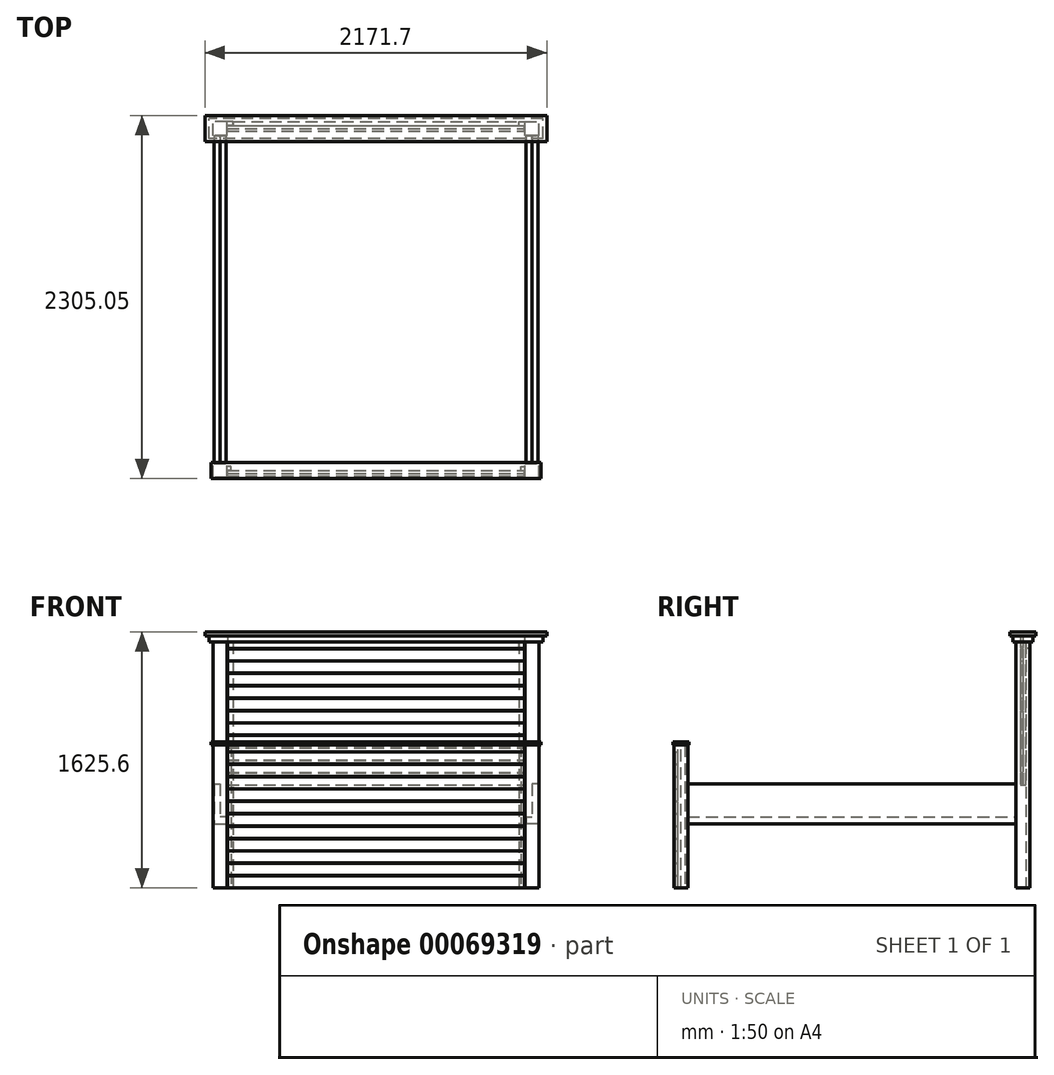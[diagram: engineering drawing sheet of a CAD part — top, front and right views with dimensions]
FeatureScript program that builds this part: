
annotation { "Feature Type Name" : "Feature", "Feature Type Description" : "" }
export const myFeature = defineFeature(function(context is Context, id is Id, definition is map)
    precondition{}
    {
        {
            var Q0;
            Q0=qCreatedBy(makeId("Top.planeOp"),FACE);
            var sketch = newSketch(context, id + "F0", { "sketchPlane" : qUnion([Q0])});
            skLineSegment(sketch, "E0.rect.bottom", {"start": v(44.45, -44.45) * mm, "end": v(-44.45, -44.45) * mm});
            skLineSegment(sketch, "E0.rect.top", {"start": v(44.45, 44.45) * mm, "end": v(-44.45, 44.45) * mm});
            skLineSegment(sketch, "E0.rect.left", {"start": v(44.45, -44.45) * mm, "end": v(44.45, 44.45) * mm});
            skLineSegment(sketch, "E0.rect.right", {"start": v(-44.45, -44.45) * mm, "end": v(-44.45, 44.45) * mm});
            skPoint(sketch, "E0.rect.middle", {"position": v(0, 0) * mm});
            skSolve(sketch);
        }
        {
            var Q0;
            Q0 = qSketchRegion(id + "F0", true);
            extrude(context, id + "F1", {"entities" : qUnion([Q0]), "depth" : 906.78 * mm});
        }
        {
            var Q0;
            Q0=makeQuery(id+"F1.opExtrude","SWEPT_FACE",FACE,{"disambiguationData":[OSD([sQuery(id+"F0.wireOp",EDGE,"E0.rect.left")])]});
            var sketch = newSketch(context, id + "F2", { "sketchPlane" : qUnion([Q0])});
            skLineSegment(sketch, "E1.bottom", {"start": v(0, 906.78) * mm, "end": v(25.4, 906.78) * mm});
            skLineSegment(sketch, "E1.top", {"start": v(0, 0) * mm, "end": v(25.4, 0) * mm});
            skLineSegment(sketch, "E1.left", {"start": v(0, 906.78) * mm, "end": v(0, 0) * mm});
            skLineSegment(sketch, "E1.right", {"start": v(25.4, 906.78) * mm, "end": v(25.4, 0) * mm});
            skSolve(sketch);
        }
        {
            var Q0;
            Q0 = qSketchRegion(id + "F2", true);
            extrude(context, id + "F3", {"entities" : qUnion([Q0]), "depth" : 25.4 * mm});
        }
        {
            var Q0;
            Q0=qCreatedBy(makeId("Right.planeOp"),FACE);
            cPlane(context, id + "F4", {"entities" : qUnion([Q0]), "cplaneType" : CPlaneType.OFFSET, "offset" : 990.6 * mm, "width" : 152.4 * mm, "height" : 152.4 * mm});
        }
        {
            var Q0;
            Q0=makeQuery(id+"F1.opExtrude","SWEPT_BODY",BODY,{"disambiguationData":[OSD([sQuery(id+"F0.wireOp",EDGE,"E0.rect.bottom"),sQuery(id+"F0.wireOp",EDGE,"E0.rect.top"),sQuery(id+"F0.wireOp",EDGE,"E0.rect.left"),sQuery(id+"F0.wireOp",EDGE,"E0.rect.right")])]});
            var Q1;
            Q1=makeQuery(id+"F3.opExtrude","SWEPT_BODY",BODY,{"disambiguationData":[OSD([sQuery(id+"F2.wireOp",EDGE,"E1.bottom"),sQuery(id+"F2.wireOp",EDGE,"E1.top"),sQuery(id+"F2.wireOp",EDGE,"E1.left"),sQuery(id+"F2.wireOp",EDGE,"E1.right")])]});
            var Q2;
            Q2=qCreatedBy(id+"F4.planeOp",FACE);
            mirror(context, id + "F5", {"entities" : qUnion([Q0, Q1]), "mirrorPlane" : qUnion([Q2])});
        }
        {
            var Q0;
            Q0=makeQuery(id+"F1.opExtrude","CAP_FACE",FACE,{"disambiguationData":[OSD([sQuery(id+"F0.wireOp",EDGE,"E0.rect.bottom"),sQuery(id+"F0.wireOp",EDGE,"E0.rect.top"),sQuery(id+"F0.wireOp",EDGE,"E0.rect.left"),sQuery(id+"F0.wireOp",EDGE,"E0.rect.right")])],"isStart":false});
            var sketch = newSketch(context, id + "F6", { "sketchPlane" : qUnion([Q0])});
            skLineSegment(sketch, "E2", {"start": v(0, 0) * mm, "end": v(1981.2, 0) * mm, "construction": true});
            skPoint(sketch, "E2.endSnap0", {"position": v(44.45, 0) * mm});
            skLineSegment(sketch, "E3", {"start": v(1936.75, 44.45) * mm, "end": v(2025.65, -44.45) * mm, "construction": true});
            skLineSegment(sketch, "E4.rect.bottom", {"start": v(-57.15, -50.8) * mm, "end": v(2038.35, -50.8) * mm});
            skLineSegment(sketch, "E4.rect.top", {"start": v(-57.15, 50.8) * mm, "end": v(2038.35, 50.8) * mm});
            skLineSegment(sketch, "E4.rect.left", {"start": v(-57.15, -50.8) * mm, "end": v(-57.15, 50.8) * mm});
            skLineSegment(sketch, "E4.rect.right", {"start": v(2038.35, -50.8) * mm, "end": v(2038.35, 50.8) * mm});
            skPoint(sketch, "E4.rect.middle", {"position": v(990.6, 0) * mm});
            skSolve(sketch);
        }
        {
            var Q0;
            Q0 = qSketchRegion(id + "F6", true);
            extrude(context, id + "F7", {"entities" : qUnion([Q0]), "depth" : 19.05 * mm});
        }
        {
            var Q0;
            Q0=makeQuery(id+"F3.opExtrude","SWEPT_FACE",FACE,{"disambiguationData":[OSD([sQuery(id+"F2.wireOp",EDGE,"E1.left")])]});
            var sketch = newSketch(context, id + "F8", { "sketchPlane" : qUnion([Q0])});
            skLineSegment(sketch, "E5", {"start": v(44.45, 906.78) * mm, "end": v(1936.75, 0) * mm, "construction": true});
            skLineSegment(sketch, "E6.rect.bottom", {"start": v(46.99, 0) * mm, "end": v(1934.2, 0) * mm});
            skLineSegment(sketch, "E6.rect.top", {"start": v(46.99, 906.78) * mm, "end": v(1934.21, 906.78) * mm});
            skLineSegment(sketch, "E6.rect.left", {"start": v(47, 0) * mm, "end": v(47, 906.78) * mm});
            skLineSegment(sketch, "E6.rect.right", {"start": v(1934.2, 0) * mm, "end": v(1934.2, 906.78) * mm});
            skPoint(sketch, "E6.rect.middle", {"position": v(990.6, 453.4) * mm});
            skSolve(sketch);
        }
        {
            var Q0;
            Q0 = qSketchRegion(id + "F8", true);
            extrude(context, id + "F9", {"entities" : qUnion([Q0]), "depth" : 19.05 * mm});
        }
        {
            var Q0;
            Q0=makeQuery(id+"F9.opExtrude","CAP_FACE",FACE,{"disambiguationData":[OSD([sQuery(id+"F8.wireOp",EDGE,"E6.rect.bottom"),sQuery(id+"F8.wireOp",EDGE,"E6.rect.top"),sQuery(id+"F8.wireOp",EDGE,"E6.rect.left"),sQuery(id+"F8.wireOp",EDGE,"E6.rect.right")])],"isStart":false});
            var sketch = newSketch(context, id + "F10", { "sketchPlane" : qUnion([Q0])});
            skLineSegment(sketch, "E7.bottom", {"start": v(46.99, 76.2) * mm, "end": v(1934.2, 76.2) * mm});
            skLineSegment(sketch, "E7.top", {"start": v(46.99, 0) * mm, "end": v(1934.2, 0) * mm});
            skLineSegment(sketch, "E7.left", {"start": v(47, 76.2) * mm, "end": v(47, 0) * mm});
            skLineSegment(sketch, "E7.right", {"start": v(1934.2, 76.2) * mm, "end": v(1934.2, 0) * mm});
            skLineSegment(sketch, "E8.0.1.0", {"start": v(47, 154.94) * mm, "end": v(47, 78.74) * mm});
            skLineSegment(sketch, "E8.0.1.1", {"start": v(46.99, 154.94) * mm, "end": v(1934.2, 154.94) * mm});
            skLineSegment(sketch, "E8.0.1.2", {"start": v(46.99, 78.74) * mm, "end": v(1934.2, 78.74) * mm});
            skLineSegment(sketch, "E8.0.1.3", {"start": v(1934.2, 154.94) * mm, "end": v(1934.2, 78.74) * mm});
            skLineSegment(sketch, "E8.0.2.0", {"start": v(47, 233.68) * mm, "end": v(47, 157.48) * mm});
            skLineSegment(sketch, "E8.0.2.1", {"start": v(46.99, 233.68) * mm, "end": v(1934.2, 233.68) * mm});
            skLineSegment(sketch, "E8.0.2.2", {"start": v(46.99, 157.48) * mm, "end": v(1934.2, 157.48) * mm});
            skLineSegment(sketch, "E8.0.2.3", {"start": v(1934.2, 233.68) * mm, "end": v(1934.2, 157.48) * mm});
            skLineSegment(sketch, "E8.0.3.0", {"start": v(47, 312.42) * mm, "end": v(47, 236.22) * mm});
            skLineSegment(sketch, "E8.0.3.1", {"start": v(46.99, 312.42) * mm, "end": v(1934.2, 312.42) * mm});
            skLineSegment(sketch, "E8.0.3.2", {"start": v(46.99, 236.22) * mm, "end": v(1934.2, 236.22) * mm});
            skLineSegment(sketch, "E8.0.3.3", {"start": v(1934.2, 312.42) * mm, "end": v(1934.2, 236.22) * mm});
            skLineSegment(sketch, "E8.0.4.0", {"start": v(47, 391.16) * mm, "end": v(47, 314.96) * mm});
            skLineSegment(sketch, "E8.0.4.1", {"start": v(46.99, 391.16) * mm, "end": v(1934.2, 391.16) * mm});
            skLineSegment(sketch, "E8.0.4.2", {"start": v(46.99, 314.96) * mm, "end": v(1934.2, 314.96) * mm});
            skLineSegment(sketch, "E8.0.4.3", {"start": v(1934.2, 391.16) * mm, "end": v(1934.2, 314.96) * mm});
            skLineSegment(sketch, "E8.0.5.0", {"start": v(47, 469.9) * mm, "end": v(47, 393.7) * mm});
            skLineSegment(sketch, "E8.0.5.1", {"start": v(46.99, 469.9) * mm, "end": v(1934.2, 469.9) * mm});
            skLineSegment(sketch, "E8.0.5.2", {"start": v(46.99, 393.7) * mm, "end": v(1934.2, 393.7) * mm});
            skLineSegment(sketch, "E8.0.5.3", {"start": v(1934.2, 469.9) * mm, "end": v(1934.2, 393.7) * mm});
            skLineSegment(sketch, "E8.direction1", {"start": v(47, 0) * mm, "end": v(72.4, 0) * mm, "construction": true});
            skLineSegment(sketch, "E8.direction2", {"start": v(47, 0) * mm, "end": v(47, 78.74) * mm, "construction": true});
            skLineSegment(sketch, "E9.0.0.6", {"start": v(47, 548.64) * mm, "end": v(47, 472.44) * mm});
            skLineSegment(sketch, "E9.3.0.6", {"start": v(46.99, 548.64) * mm, "end": v(1934.2, 548.64) * mm});
            skLineSegment(sketch, "E9.6.0.6", {"start": v(46.99, 472.44) * mm, "end": v(1934.2, 472.44) * mm});
            skLineSegment(sketch, "E9.9.0.6", {"start": v(1934.2, 548.64) * mm, "end": v(1934.2, 472.44) * mm});
            skLineSegment(sketch, "E10.0.0.7", {"start": v(47, 627.38) * mm, "end": v(47, 551.18) * mm});
            skLineSegment(sketch, "E10.3.0.7", {"start": v(46.99, 627.38) * mm, "end": v(1934.2, 627.38) * mm});
            skLineSegment(sketch, "E10.6.0.7", {"start": v(46.99, 551.18) * mm, "end": v(1934.2, 551.18) * mm});
            skLineSegment(sketch, "E10.9.0.7", {"start": v(1934.2, 627.38) * mm, "end": v(1934.2, 551.18) * mm});
            skLineSegment(sketch, "E10.0.0.8", {"start": v(47, 706.12) * mm, "end": v(47, 629.92) * mm});
            skLineSegment(sketch, "E10.3.0.8", {"start": v(46.99, 706.12) * mm, "end": v(1934.2, 706.12) * mm});
            skLineSegment(sketch, "E10.6.0.8", {"start": v(46.99, 629.92) * mm, "end": v(1934.2, 629.92) * mm});
            skLineSegment(sketch, "E10.9.0.8", {"start": v(1934.2, 706.12) * mm, "end": v(1934.2, 629.92) * mm});
            skLineSegment(sketch, "E10.0.0.9", {"start": v(47, 784.86) * mm, "end": v(47, 708.66) * mm});
            skLineSegment(sketch, "E10.3.0.9", {"start": v(46.99, 784.86) * mm, "end": v(1934.2, 784.86) * mm});
            skLineSegment(sketch, "E10.6.0.9", {"start": v(46.99, 708.66) * mm, "end": v(1934.2, 708.66) * mm});
            skLineSegment(sketch, "E10.9.0.9", {"start": v(1934.2, 784.86) * mm, "end": v(1934.2, 708.66) * mm});
            skLineSegment(sketch, "E11.0.0.10", {"start": v(47, 863.6) * mm, "end": v(47, 787.4) * mm});
            skLineSegment(sketch, "E11.3.0.10", {"start": v(46.99, 863.6) * mm, "end": v(1934.2, 863.6) * mm});
            skLineSegment(sketch, "E11.6.0.10", {"start": v(46.99, 787.4) * mm, "end": v(1934.2, 787.4) * mm});
            skLineSegment(sketch, "E11.9.0.10", {"start": v(1934.2, 863.6) * mm, "end": v(1934.2, 787.4) * mm});
            skSolve(sketch);
        }
        {
            var Q0;
            Q0 = qSketchRegion(id + "F10", true);
            extrude(context, id + "F11", {"entities" : qUnion([Q0]), "depth" : 15.88 * mm});
        }
        {
            var Q0;
            Q0=makeQuery(id+"F1.opExtrude","SWEPT_FACE",FACE,{"disambiguationData":[OSD([sQuery(id+"F0.wireOp",EDGE,"E0.rect.top")])]});
            var sketch = newSketch(context, id + "F12", { "sketchPlane" : qUnion([Q0])});
            skLineSegment(sketch, "E12.bottom", {"start": v(38.1, 660.4) * mm, "end": v(0, 660.4) * mm});
            skLineSegment(sketch, "E12.top", {"start": v(38.1, 406.4) * mm, "end": v(0, 406.4) * mm});
            skLineSegment(sketch, "E12.left", {"start": v(38.1, 660.4) * mm, "end": v(38.1, 406.4) * mm});
            skLineSegment(sketch, "E12.right", {"start": v(0, 660.4) * mm, "end": v(0, 406.4) * mm});
            skSolve(sketch);
        }
        {
            var Q0;
            Q0 = qSketchRegion(id + "F12", true);
            extrude(context, id + "F13", {"entities" : qUnion([Q0]), "depth" : 2082.8 * mm});
        }
        {
            var Q0;
            Q0=makeQuery(id+"F13.opExtrude","SWEPT_FACE",FACE,{"disambiguationData":[OSD([sQuery(id+"F12.wireOp",EDGE,"E12.right")])]});
            var sketch = newSketch(context, id + "F14", { "sketchPlane" : qUnion([Q0])});
            skLineSegment(sketch, "E13.bottom", {"start": v(44.45, 450.85) * mm, "end": v(2127.25, 450.85) * mm});
            skLineSegment(sketch, "E13.top", {"start": v(44.45, 406.4) * mm, "end": v(2127.25, 406.4) * mm});
            skLineSegment(sketch, "E13.left", {"start": v(44.45, 450.85) * mm, "end": v(44.45, 406.4) * mm});
            skLineSegment(sketch, "E13.right", {"start": v(2127.25, 450.85) * mm, "end": v(2127.25, 406.4) * mm});
            skSolve(sketch);
        }
        {
            var Q0;
            Q0 = qSketchRegion(id + "F14", true);
            extrude(context, id + "F15", {"entities" : qUnion([Q0]), "depth" : 38.1 * mm});
        }
        {
            var Q0;
            Q0=makeQuery(id+"F13.opExtrude","SWEPT_BODY",BODY,{"disambiguationData":[OSD([sQuery(id+"F12.wireOp",EDGE,"E12.bottom"),sQuery(id+"F12.wireOp",EDGE,"E12.top"),sQuery(id+"F12.wireOp",EDGE,"E12.left"),sQuery(id+"F12.wireOp",EDGE,"E12.right")])]});
            var Q1;
            Q1=makeQuery(id+"F15.opExtrude","SWEPT_BODY",BODY,{"disambiguationData":[OSD([sQuery(id+"F14.wireOp",EDGE,"E13.bottom"),sQuery(id+"F14.wireOp",EDGE,"E13.top"),sQuery(id+"F14.wireOp",EDGE,"E13.left"),sQuery(id+"F14.wireOp",EDGE,"E13.right")])]});
            var Q2;
            Q2=qCreatedBy(id+"F4.planeOp",FACE);
            mirror(context, id + "F16", {"operationType" : NewBodyOperationType.ADD, "entities" : qUnion([Q0, Q1]), "mirrorPlane" : qUnion([Q2])});
        }
        {
            var Q0;
            Q0=qCreatedBy(makeId("Top.planeOp"),FACE);
            var sketch = newSketch(context, id + "F17", { "sketchPlane" : qUnion([Q0])});
            skLineSegment(sketch, "E14.rect.bottom", {"start": v(44.45, 2127.25) * mm, "end": v(-44.45, 2127.25) * mm});
            skLineSegment(sketch, "E14.rect.top", {"start": v(44.45, 2216.15) * mm, "end": v(-44.45, 2216.15) * mm});
            skLineSegment(sketch, "E14.rect.left", {"start": v(44.45, 2127.25) * mm, "end": v(44.45, 2216.15) * mm});
            skLineSegment(sketch, "E14.rect.right", {"start": v(-44.45, 2127.25) * mm, "end": v(-44.45, 2216.15) * mm});
            skPoint(sketch, "E14.rect.middle", {"position": v(0, 2171.7) * mm});
            skLineSegment(sketch, "E15.rect.bottom", {"start": v(1936.75, 2127.25) * mm, "end": v(2025.65, 2127.25) * mm});
            skLineSegment(sketch, "E15.rect.top", {"start": v(1936.75, 2216.15) * mm, "end": v(2025.65, 2216.15) * mm});
            skLineSegment(sketch, "E15.rect.left", {"start": v(1936.75, 2127.25) * mm, "end": v(1936.75, 2216.15) * mm});
            skLineSegment(sketch, "E15.rect.right", {"start": v(2025.65, 2127.25) * mm, "end": v(2025.65, 2216.15) * mm});
            skPoint(sketch, "E15.rect.middle", {"position": v(1981.2, 2171.7) * mm});
            skSolve(sketch);
        }
        {
            var Q0;
            Q0 = qSketchRegion(id + "F17", true);
            extrude(context, id + "F18", {"entities" : qUnion([Q0]), "depth" : 1562.1 * mm});
        }
        {
            var Q0;
            Q0=makeQuery(id+"F18.opExtrude","SWEPT_FACE",FACE,{"disambiguationData":[OSD([sQuery(id+"F17.wireOp",EDGE,"E14.rect.left")])]});
            var sketch = newSketch(context, id + "F19", { "sketchPlane" : qUnion([Q0])});
            skLineSegment(sketch, "E16.bottom", {"start": v(2216.15, 1562.1) * mm, "end": v(2190.75, 1562.1) * mm});
            skLineSegment(sketch, "E16.top", {"start": v(2216.15, 0) * mm, "end": v(2171.7, 0) * mm});
            skLineSegment(sketch, "E16.left", {"start": v(2216.15, 1562.1) * mm, "end": v(2216.15, 0) * mm});
            skLineSegment(sketch, "E16.right", {"start": v(2190.75, 1562.1) * mm, "end": v(2190.75, 0) * mm});
            skSolve(sketch);
        }
        {
            var Q0;
            Q0 = qSketchRegion(id + "F19", true);
            extrude(context, id + "F20", {"entities" : qUnion([Q0]), "depth" : 38.1 * mm});
        }
        {
            var Q0;
            Q0=makeQuery(id+"F20.opExtrude","SWEPT_BODY",BODY,{"disambiguationData":[OSD([sQuery(id+"F19.wireOp",EDGE,"E16.bottom"),sQuery(id+"F19.wireOp",EDGE,"E16.top"),sQuery(id+"F19.wireOp",EDGE,"E16.left"),sQuery(id+"F19.wireOp",EDGE,"E16.right")])]});
            var Q1;
            Q1=qCreatedBy(id+"F4.planeOp",FACE);
            mirror(context, id + "F21", {"entities" : qUnion([Q0]), "mirrorPlane" : qUnion([Q1])});
        }
        {
            var Q0;
            Q0=makeQuery(id+"F18.opExtrude","CAP_FACE",FACE,{"disambiguationData":[OSD([sQuery(id+"F17.wireOp",EDGE,"E14.rect.bottom"),sQuery(id+"F17.wireOp",EDGE,"E14.rect.top"),sQuery(id+"F17.wireOp",EDGE,"E14.rect.left"),sQuery(id+"F17.wireOp",EDGE,"E14.rect.right")])],"isStart":false});
            var sketch = newSketch(context, id + "F22", { "sketchPlane" : qUnion([Q0])});
            skLineSegment(sketch, "E17", {"start": v(44.45, 2171.7) * mm, "end": v(1936.75, 2171.7) * mm, "construction": true});
            skPoint(sketch, "E17.endSnap0", {"position": v(44.45, 2171.7) * mm});
            skLineSegment(sketch, "E18.rect.bottom", {"start": v(2051.05, 2108.2) * mm, "end": v(-69.85, 2108.2) * mm});
            skLineSegment(sketch, "E18.rect.top", {"start": v(2051.05, 2235.2) * mm, "end": v(-69.85, 2235.2) * mm});
            skLineSegment(sketch, "E18.rect.left", {"start": v(2051.05, 2108.2) * mm, "end": v(2051.05, 2235.2) * mm});
            skLineSegment(sketch, "E18.rect.right", {"start": v(-69.85, 2108.2) * mm, "end": v(-69.85, 2235.2) * mm});
            skPoint(sketch, "E18.rect.middle", {"position": v(990.6, 2171.7) * mm});
            skSolve(sketch);
        }
        {
            var Q0;
            Q0 = qSketchRegion(id + "F22", true);
            extrude(context, id + "F23", {"entities" : qUnion([Q0]), "depth" : 38.1 * mm});
        }
        {
            var Q0;
            Q0=makeQuery(id+"F23.opExtrude","CAP_FACE",FACE,{"disambiguationData":[OSD([sQuery(id+"F22.wireOp",EDGE,"E18.rect.bottom"),sQuery(id+"F22.wireOp",EDGE,"E18.rect.top"),sQuery(id+"F22.wireOp",EDGE,"E18.rect.left"),sQuery(id+"F22.wireOp",EDGE,"E18.rect.right")])],"isStart":true});
            var sketch = newSketch(context, id + "F24", { "sketchPlane" : qUnion([Q0])});
            skLineSegment(sketch, "E19.bottom", {"start": v(85.1, -2190.75) * mm, "end": v(1898.65, -2190.75) * mm});
            skLineSegment(sketch, "E19.top", {"start": v(85.1, -2216.15) * mm, "end": v(1898.65, -2216.15) * mm});
            skLineSegment(sketch, "E19.left", {"start": v(85.1, -2190.75) * mm, "end": v(85.1, -2216.15) * mm});
            skLineSegment(sketch, "E19.right", {"start": v(1898.65, -2190.75) * mm, "end": v(1898.65, -2216.15) * mm});
            skSolve(sketch);
        }
        {
            var Q0;
            Q0 = qSketchRegion(id + "F24", true);
            extrude(context, id + "F25", {"entities" : qUnion([Q0]), "depth" : 38.1 * mm});
        }
        {
            var Q0;
            Q0=makeQuery(id+"F20.opExtrude","SWEPT_FACE",FACE,{"disambiguationData":[OSD([sQuery(id+"F19.wireOp",EDGE,"E16.right")])]});
            var sketch = newSketch(context, id + "F26", { "sketchPlane" : qUnion([Q0])});
            skLineSegment(sketch, "E20", {"start": v(44.45, 1562.1) * mm, "end": v(1936.75, 654.05) * mm, "construction": true});
            skLineSegment(sketch, "E21.rect.bottom", {"start": v(46.04, 655.64) * mm, "end": v(1935.16, 655.64) * mm});
            skLineSegment(sketch, "E21.rect.top", {"start": v(46.04, 1560.51) * mm, "end": v(1935.16, 1560.51) * mm});
            skLineSegment(sketch, "E21.rect.left", {"start": v(46.04, 655.64) * mm, "end": v(46.04, 1560.51) * mm});
            skLineSegment(sketch, "E21.rect.right", {"start": v(1935.16, 655.64) * mm, "end": v(1935.16, 1560.51) * mm});
            skPoint(sketch, "E21.rect.middle", {"position": v(990.6, 1108.07) * mm});
            skSolve(sketch);
        }
        {
            var Q0;
            Q0 = qSketchRegion(id + "F26", true);
            extrude(context, id + "F27", {"entities" : qUnion([Q0]), "depth" : 19.05 * mm});
        }
        {
            var Q0;
            Q0=makeQuery(id+"F27.opExtrude","CAP_FACE",FACE,{"disambiguationData":[OSD([sQuery(id+"F26.wireOp",EDGE,"E21.rect.bottom"),sQuery(id+"F26.wireOp",EDGE,"E21.rect.top"),sQuery(id+"F26.wireOp",EDGE,"E21.rect.left"),sQuery(id+"F26.wireOp",EDGE,"E21.rect.right")])],"isStart":false});
            var sketch = newSketch(context, id + "F28", { "sketchPlane" : qUnion([Q0])});
            skLineSegment(sketch, "E22.bottom", {"start": v(47, 731.84) * mm, "end": v(1934.21, 731.84) * mm});
            skLineSegment(sketch, "E22.top", {"start": v(46.99, 655.64) * mm, "end": v(1934.21, 655.64) * mm});
            skLineSegment(sketch, "E22.left", {"start": v(46.99, 731.84) * mm, "end": v(46.99, 655.64) * mm});
            skLineSegment(sketch, "E22.right", {"start": v(1934.21, 731.84) * mm, "end": v(1934.21, 655.64) * mm});
            skLineSegment(sketch, "E23.0.1.0", {"start": v(46.99, 810.58) * mm, "end": v(1934.21, 810.58) * mm});
            skLineSegment(sketch, "E23.0.1.1", {"start": v(1934.21, 810.58) * mm, "end": v(1934.21, 734.38) * mm});
            skLineSegment(sketch, "E23.0.1.2", {"start": v(47, 734.38) * mm, "end": v(1934.21, 734.38) * mm});
            skLineSegment(sketch, "E23.0.1.3", {"start": v(46.99, 810.58) * mm, "end": v(46.99, 734.38) * mm});
            skLineSegment(sketch, "E23.0.2.0", {"start": v(46.99, 889.32) * mm, "end": v(1934.21, 889.32) * mm});
            skLineSegment(sketch, "E23.0.2.1", {"start": v(1934.21, 889.32) * mm, "end": v(1934.21, 813.12) * mm});
            skLineSegment(sketch, "E23.0.2.2", {"start": v(47, 813.12) * mm, "end": v(1934.21, 813.12) * mm});
            skLineSegment(sketch, "E23.0.2.3", {"start": v(46.99, 889.32) * mm, "end": v(46.99, 813.12) * mm});
            skLineSegment(sketch, "E23.0.3.0", {"start": v(46.99, 968.06) * mm, "end": v(1934.21, 968.06) * mm});
            skLineSegment(sketch, "E23.0.3.1", {"start": v(1934.21, 968.06) * mm, "end": v(1934.21, 891.86) * mm});
            skLineSegment(sketch, "E23.0.3.2", {"start": v(47, 891.86) * mm, "end": v(1934.21, 891.86) * mm});
            skLineSegment(sketch, "E23.0.3.3", {"start": v(46.99, 968.06) * mm, "end": v(46.99, 891.86) * mm});
            skLineSegment(sketch, "E23.0.4.0", {"start": v(46.99, 1046.8) * mm, "end": v(1934.21, 1046.8) * mm});
            skLineSegment(sketch, "E23.0.4.1", {"start": v(1934.21, 1046.8) * mm, "end": v(1934.21, 970.6) * mm});
            skLineSegment(sketch, "E23.0.4.2", {"start": v(47, 970.6) * mm, "end": v(1934.21, 970.6) * mm});
            skLineSegment(sketch, "E23.0.4.3", {"start": v(46.99, 1046.8) * mm, "end": v(46.99, 970.6) * mm});
            skLineSegment(sketch, "E23.0.5.0", {"start": v(46.99, 1125.54) * mm, "end": v(1934.21, 1125.54) * mm});
            skLineSegment(sketch, "E23.0.5.1", {"start": v(1934.21, 1125.54) * mm, "end": v(1934.21, 1049.34) * mm});
            skLineSegment(sketch, "E23.0.5.2", {"start": v(47, 1049.34) * mm, "end": v(1934.21, 1049.34) * mm});
            skLineSegment(sketch, "E23.0.5.3", {"start": v(46.99, 1125.54) * mm, "end": v(46.99, 1049.34) * mm});
            skLineSegment(sketch, "E23.direction1", {"start": v(47, 731.84) * mm, "end": v(72.39, 731.84) * mm, "construction": true});
            skLineSegment(sketch, "E23.direction2", {"start": v(46.99, 731.84) * mm, "end": v(46.99, 810.58) * mm, "construction": true});
            skLineSegment(sketch, "E24.0.0.6", {"start": v(46.99, 1204.28) * mm, "end": v(1934.21, 1204.28) * mm});
            skLineSegment(sketch, "E24.3.0.6", {"start": v(1934.21, 1204.28) * mm, "end": v(1934.21, 1128.08) * mm});
            skLineSegment(sketch, "E24.6.0.6", {"start": v(47, 1128.08) * mm, "end": v(1934.21, 1128.08) * mm});
            skLineSegment(sketch, "E24.9.0.6", {"start": v(46.99, 1204.28) * mm, "end": v(46.99, 1128.08) * mm});
            skLineSegment(sketch, "E25.0.0.7", {"start": v(46.99, 1283.02) * mm, "end": v(1934.21, 1283.02) * mm});
            skLineSegment(sketch, "E25.3.0.7", {"start": v(1934.21, 1283.02) * mm, "end": v(1934.21, 1206.82) * mm});
            skLineSegment(sketch, "E25.6.0.7", {"start": v(47, 1206.82) * mm, "end": v(1934.21, 1206.82) * mm});
            skLineSegment(sketch, "E25.9.0.7", {"start": v(46.99, 1283.02) * mm, "end": v(46.99, 1206.82) * mm});
            skLineSegment(sketch, "E25.0.0.8", {"start": v(46.99, 1361.76) * mm, "end": v(1934.21, 1361.76) * mm});
            skLineSegment(sketch, "E25.3.0.8", {"start": v(1934.21, 1361.76) * mm, "end": v(1934.21, 1285.56) * mm});
            skLineSegment(sketch, "E25.6.0.8", {"start": v(46.99, 1285.56) * mm, "end": v(1934.2, 1285.56) * mm});
            skLineSegment(sketch, "E25.9.0.8", {"start": v(46.99, 1361.76) * mm, "end": v(46.99, 1285.56) * mm});
            skLineSegment(sketch, "E25.0.0.9", {"start": v(46.99, 1440.5) * mm, "end": v(1934.21, 1440.5) * mm});
            skLineSegment(sketch, "E25.3.0.9", {"start": v(1934.21, 1440.5) * mm, "end": v(1934.21, 1364.3) * mm});
            skLineSegment(sketch, "E25.6.0.9", {"start": v(46.99, 1364.3) * mm, "end": v(1934.2, 1364.3) * mm});
            skLineSegment(sketch, "E25.9.0.9", {"start": v(46.99, 1440.5) * mm, "end": v(46.99, 1364.3) * mm});
            skLineSegment(sketch, "E25.0.0.10", {"start": v(46.99, 1519.24) * mm, "end": v(1934.21, 1519.24) * mm});
            skLineSegment(sketch, "E25.3.0.10", {"start": v(1934.21, 1519.24) * mm, "end": v(1934.21, 1443.04) * mm});
            skLineSegment(sketch, "E25.6.0.10", {"start": v(46.99, 1443.04) * mm, "end": v(1934.2, 1443.04) * mm});
            skLineSegment(sketch, "E25.9.0.10", {"start": v(46.99, 1519.24) * mm, "end": v(46.99, 1443.04) * mm});
            skLineSegment(sketch, "E25.0.0.11", {"start": v(46.99, 1597.98) * mm, "end": v(1934.21, 1597.98) * mm});
            skLineSegment(sketch, "E25.3.0.11", {"start": v(1934.21, 1597.98) * mm, "end": v(1934.21, 1521.78) * mm});
            skLineSegment(sketch, "E25.6.0.11", {"start": v(46.99, 1521.78) * mm, "end": v(1934.2, 1521.78) * mm});
            skLineSegment(sketch, "E25.9.0.11", {"start": v(46.99, 1597.98) * mm, "end": v(46.99, 1521.78) * mm});
            skSolve(sketch);
        }
        {
            var Q0;
            Q0 = qSketchRegion(id + "F28", true);
            extrude(context, id + "F29", {"entities" : qUnion([Q0]), "depth" : 15.88 * mm});
        }
        {
            var Q0;
            Q0=makeQuery(id+"F23.opExtrude","CAP_FACE",FACE,{"disambiguationData":[OSD([sQuery(id+"F22.wireOp",EDGE,"E18.rect.bottom"),sQuery(id+"F22.wireOp",EDGE,"E18.rect.top"),sQuery(id+"F22.wireOp",EDGE,"E18.rect.left"),sQuery(id+"F22.wireOp",EDGE,"E18.rect.right")])],"isStart":false});
            var sketch = newSketch(context, id + "F30", { "sketchPlane" : qUnion([Q0])});
            skLineSegment(sketch, "E26", {"start": v(990.6, 2235.2) * mm, "end": v(990.6, 2108.2) * mm, "construction": true});
            skLineSegment(sketch, "E27.rect.bottom", {"start": v(-95.25, 2089.15) * mm, "end": v(2076.45, 2089.15) * mm});
            skLineSegment(sketch, "E27.rect.top", {"start": v(-95.25, 2254.25) * mm, "end": v(2076.45, 2254.25) * mm});
            skLineSegment(sketch, "E27.rect.left", {"start": v(-95.25, 2089.15) * mm, "end": v(-95.25, 2254.25) * mm});
            skLineSegment(sketch, "E27.rect.right", {"start": v(2076.45, 2089.15) * mm, "end": v(2076.45, 2254.25) * mm});
            skPoint(sketch, "E27.rect.middle", {"position": v(990.6, 2171.7) * mm});
            skSolve(sketch);
        }
        {
            var Q0;
            Q0 = qSketchRegion(id + "F30", true);
            var Q1;
            Q1 = qConstructionFilter(qBodyType(qCreatedBy(id + "F30" ,EDGE), BodyType.WIRE), ConstructionObject.NO);
            extrude(context, id + "F31", {"entities" : qUnion([Q0]), "surfaceEntities" : qUnion([Q1]), "depth" : 25.4 * mm});
        }
    });
